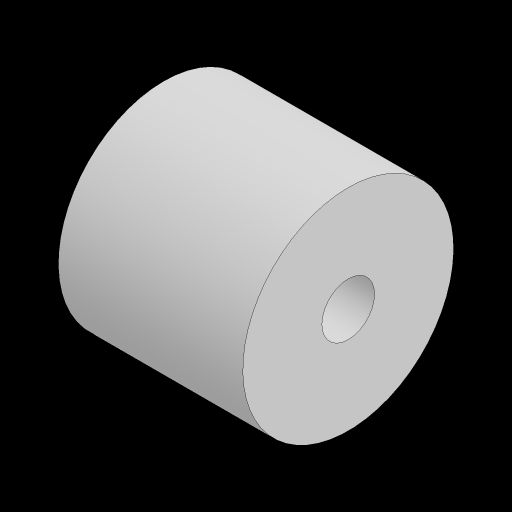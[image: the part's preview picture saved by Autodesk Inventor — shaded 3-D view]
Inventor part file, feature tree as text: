
AUTODESK INVENTOR PART (.ipt)
format: ipt  version: 2023.2 (Build 272271030, 271C)  size: 111,616 bytes
history: native  units: mm
features: revolve x1, sketch x1
ambient origin geometry x8: Origin, YZ Plane, XZ Plane, XY Plane, X Axis, Y Axis, Z Axis, Center Point
bodies: Solid1 (feature_tree)
feature tree (2):
  revolve  "Revolution1"  [1 undecoded]
  sketch  "Sketch1"  dims[d0=4.0mm d1=2.25mm d2=1.0mm d3=3.0mm d4=4.0mm d5=90.0deg]
note: 1 required parameter value undecoded (feature->parameter linkage not recoverable at this tier; creation-order binding heuristic only, values carry confidence <= 0.55)
